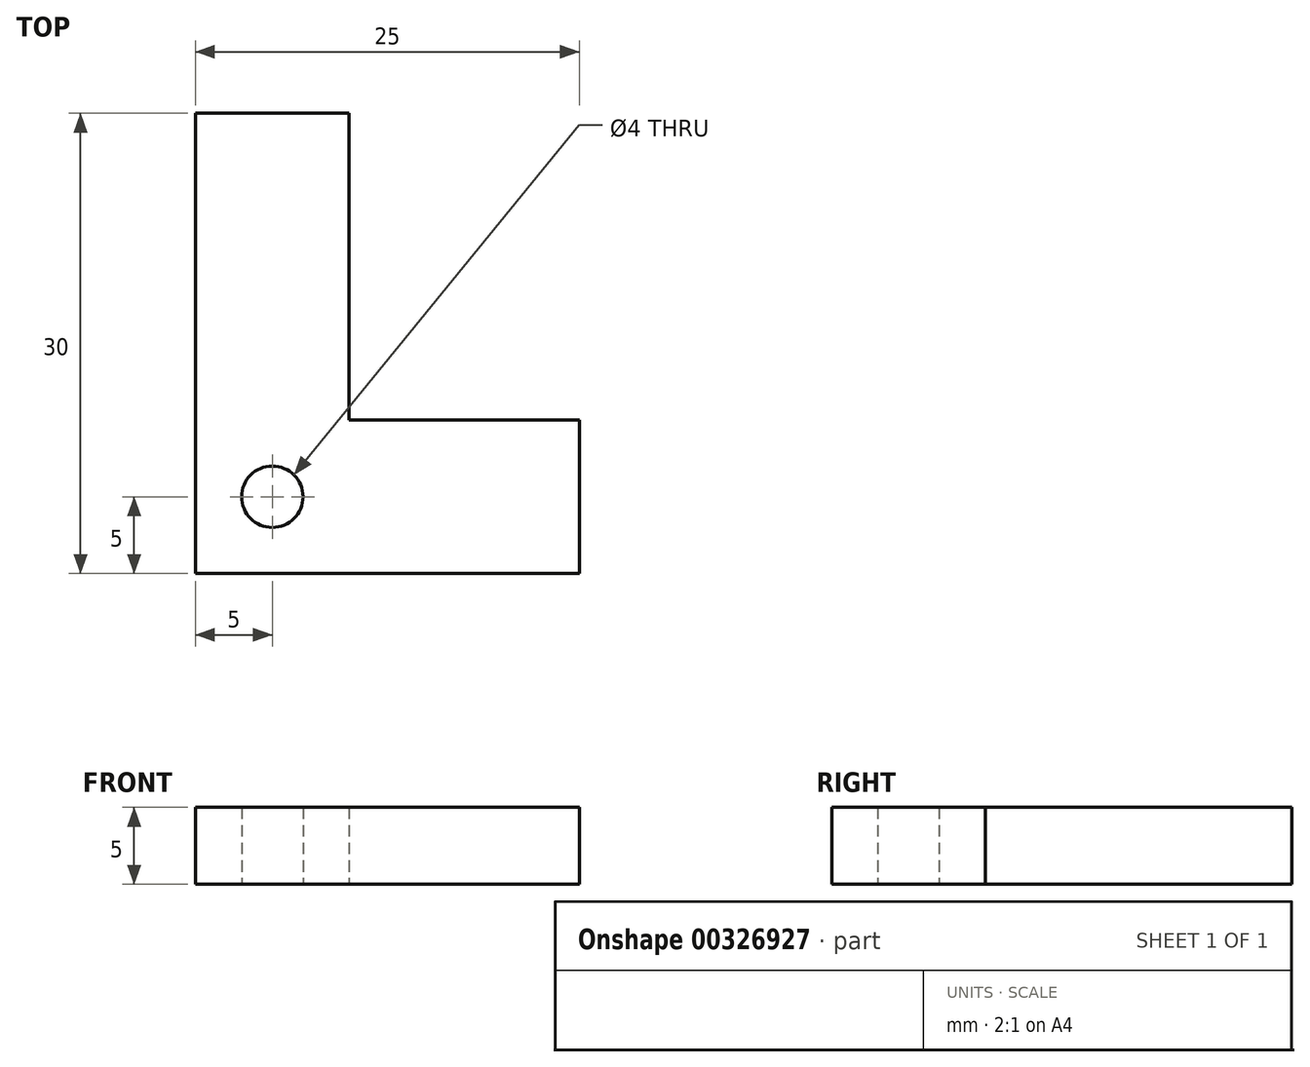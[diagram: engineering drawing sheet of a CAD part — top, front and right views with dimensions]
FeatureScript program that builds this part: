
annotation { "Feature Type Name" : "Feature", "Feature Type Description" : "" }
export const myFeature = defineFeature(function(context is Context, id is Id, definition is map)
    precondition{}
    {
        {
            var Q0;
            Q0=qCreatedBy(makeId("Top.planeOp"),FACE);
            var sketch = newSketch(context, id + "F0", { "sketchPlane" : qUnion([Q0])});
            skLineSegment(sketch, "E0", {"start": v(0, 0) * mm, "end": v(15, 0) * mm});
            skLineSegment(sketch, "E1", {"start": v(0, 0) * mm, "end": v(0, 20) * mm});
            skLineSegment(sketch, "E2", {"start": v(15, 0) * mm, "end": v(15, -10) * mm});
            skLineSegment(sketch, "E3", {"start": v(0, 20) * mm, "end": v(-10, 20) * mm});
            skLineSegment(sketch, "E4", {"start": v(15, -10) * mm, "end": v(-41.04, -10) * mm, "construction": true});
            skLineSegment(sketch, "E5", {"start": v(-10, 20) * mm, "end": v(-10, -25.47) * mm, "construction": true});
            skLineSegment(sketch, "E6", {"start": v(-10, 20) * mm, "end": v(-10, -10) * mm});
            skLineSegment(sketch, "E7", {"start": v(15, -10) * mm, "end": v(-10, -10) * mm});
            skLineSegment(sketch, "E8", {"start": v(0, 0) * mm, "end": v(-10, -10) * mm, "construction": true});
            skPoint(sketch, "E9", {"position": v(-5, -5) * mm});
            skCircle(sketch, "E10", {"center": v(-5, -5) * mm, "radius": 2 * mm});
            skSolve(sketch);
        }
        {
            var Q0;
            Q0=makeQuery(id+"F0.imprint","IMPRINT",FACE,{"disambiguationData":[TD([[makeQuery(id+"F0.imprint","IMPRINT",EDGE,{"derivedFrom":sQuery(id+"F0.wireOp",EDGE,"E0")}),-1.0]])]});
            extrude(context, id + "F1", {"entities" : qUnion([Q0]), "depth" : 5 * mm});
        }
    });
